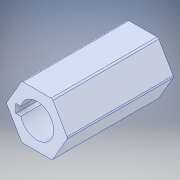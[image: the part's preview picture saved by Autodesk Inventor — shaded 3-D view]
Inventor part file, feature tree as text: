
AUTODESK INVENTOR PART (.ipt)
format: ipt  version: 2017 (Build 210142000, 142)  size: 109,056 bytes
history: native  units: in
note: dims shown in document units (in); Inventor stores cm internally (conversion verified against a paired STEP export)
features: fillet x1
ambient origin geometry x8: Origin, YZ Plane, XZ Plane, XY Plane, X Axis, Y Axis, Z Axis, Center Point
bodies: Solid1 (feature_tree)
feature tree (1):
  fillet  "Fillet1"  [1 undecoded]
note: 1 required parameter value undecoded (feature->parameter linkage not recoverable at this tier; creation-order binding heuristic only, values carry confidence <= 0.55)
